# Revit family: NBS_Allermuir_DmstcChrs_Tarry_Footstool
name_source: partatom
category: Furniture
revit_build: Autodesk Revit 2017 (Build: 20171027_0315(x64)
units: mm (PartAtom-declared; Revit-internal decimal feet)

## family parameters
Always vertical = Yes
Cut with Voids When Loaded = No
Room Calculation Point = No
Shared = No
Work Plane-Based = No

## types (2) — shared parameters
AssetType = Movable
Category = Pr_40_50_12_22:Dining chairs
DurationUnit = year
ExpectedLife = 10
IfcExportAs = IfcFurnitureType
IfcExportType = CHAIR
IsBuiltIn = No
ManufacturerName = Allermuir
ManufacturerURL = http://www.allermuir.co.uk
ModelReference = Tarry Footstool
NBSCertification = www.nationalbimlibrary.com/cert/3ns04hvb
NBSDescription = Domestic chairs
NBSReference = 45-35-20/365
NominalHeight = 410 mm  [stored 1.34514 ft]
NominalLength = 615 mm  [stored 2.01772 ft]
NominalWidth = 615 mm  [stored 2.01772 ft]
ProductInformation = http://www.allermuir.co.uk
SeatBaseMaterial = NBS_Concept
SeatingHeight = 410 mm  [stored 1.34514 ft]
SeatingSeatMaterial = NBS_Concept
SeatsAndBacksFinish = Upholstered
SeatsAndBacksMaterial = Upholstered
Status = New
Style = Footstool
Uniclass2015Code = Pr_40_50_12_22
Uniclass2015Title = Dining chairs
Uniclass2015Version = Products v1.12
Version = 1
WarrantyDescription = Allermuir warrant that its manufactured products are free from manufacturing defects - in materials or workmanship - for a period of five (5) years. , Allermuir will repair, or replace (at Allermuir's sole discretion) with comparable free of charge materials / components, any product / component which fails under normal use in a single shift environment, as a result of a defect in the materials and/ or workmanship
WarrantyDurationParts = 5
WarrantyDurationUnit = year
zero-valued in all types: HighestSeatingHeight, LowestSeatingHeight

## per-type parameters (varying)
| type | BIMObjectName | Description | Features | FramesColour | FramesFinish | FramesMaterial | Has4StarBase | HasWoodLegs | Name | NominalDepth | Size |
| TARFS03 | NBS_Allermuir_DomesticChairs_Tarry_Footstool_TARFS03 | Footstool on a four star base | Fully upholstered, solid ash legs with a clear finish, plastic glides, optional feature: solid ash legs can be stained or colour washed , optional feature: plastic glides with felt, optional feature: two-tone upholstery |  | Clear | Solid ash | No | Yes | DomesticChairs_TarryFootstool_TARFS03_Allermuir | 460 mm  [stored 1.50919 ft] | 615 x 410 x 460 mm |
| TARFS05 | NBS_Allermuir_DomesticChairs_Tarry_Footstool_TARFS05 | Footstool with wood legs | Fully upholstered, 4 star blade base finished in black powder coat, plastic glides, optional feature: 4 star blade base finished in lack powder coat, optional feature: solid ash legs can be stained or colour washed , optional feature: plastic glides with felt, optional feature: auto return swivel, optional feature: two-tone upholstery | Black | Powder coat | Steel powder coated | Yes | No | DomesticChairs_TarryFootstool_TARFS05_Allermuir | 495 mm  [stored 1.62402 ft] | 615 x 410 x 495 mm |

note: column(s) folded — value = type name in every type: ModelNumber

note: [stored X ft] marks values corroborated as IEEE doubles in the binary element streams (Revit-internal decimal feet)

## geometry (parser evidence)
native form markers: Sweep x2
no freeform markers — native parametric forms only
